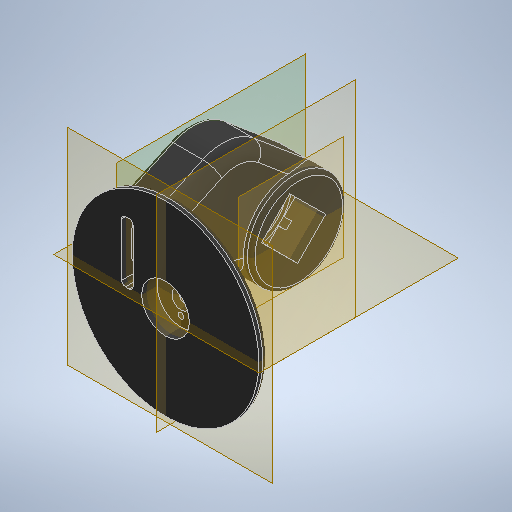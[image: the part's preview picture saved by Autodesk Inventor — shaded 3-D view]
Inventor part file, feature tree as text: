
AUTODESK INVENTOR PART (.ipt)
format: ipt  version: 2025.1 (Build 291241020, 241B)  size: 604,160 bytes
history: native  units: mm
features: extrude x18, sketch x17, projected_geometry x6, fillet x5, plane x2, revolve x1, chamfer x1
ambient origin geometry x8: Origin, YZ Plane, XZ Plane, XY Plane, X Axis, Y Axis, Z Axis, Center Point
bodies: Body1 (feature_tree), Body2 (feature_tree)
feature tree (50):
  extrude  "Extrusion6"  Depth=5.0mm TaperAngle=0.0deg
  extrude  "Extrusion15"  Depth=35.0mm
  extrude  "Extrusion16"  Depth=8.1mm TaperAngle=0.0deg
  extrude  "Extrusion17"  Depth=3.0mm
  revolve  "Revolution2"  [1 undecoded]
  fillet  "Fillet8"  Radius=4.75mm
  extrude  "Extrusion18"  Depth=3.0mm
  plane  "Work Plane5"
  extrude  "Extrusion19"  Depth=65.0mm
  extrude  "Extrusion20"  [1 undecoded]
  extrude  "Extrusion21"  Depth=10.0mm TaperAngle=0.0deg
  extrude  "Extrusion22"  Depth=35.0mm
  extrude  "Extrusion23"  Depth=20.071286mm
  extrude  "Extrusion24"  Depth=10.0mm TaperAngle=0.0deg
  extrude  "Extrusion25"  Depth=15.0mm
  extrude  "Extrusion26"  Depth=10.0mm
  sketch  "Sketch30"  dims[d126=42.0mm d128=36.0mm]
  extrude  "Extrusion27"  Depth=36.0mm
  extrude  "Extrusion28"  Depth=15.0mm
  plane  "Work Plane6"
  extrude  "Extrusion29"  Depth=2.0mm
  fillet  "Fillet9"  Radius=21.0mm
  chamfer  "Chamfer2"  Distance=7.9mm
  fillet  "Fillet10"  Radius=11.0mm
  fillet  "Fillet11"  Radius=10.0mm
  sketch  "Sketch32"  dims[d132=12.5mm d133=0.0mm d135=41.0mm d136=21.0mm d137=7.9mm d138=11.0mm d139=10.0mm d140=0.0mm d141=14.253mm d142=0.0mm d143=0.0mm d144=10.0mm d145=2.6mm d146=3.5mm d147=4.0mm d148=7.5mm d149=4.0mm d150=0.0mm d151=7.5mm d152=0.0mm d153=-2.5mm d154=2.5mm d155=2.0mm d156=0.0mm d157=5.6mm d158=2.0mm d159=45.0deg d160=7.0mm d161=2.0mm d162=7.0mm d165=1.0mm d166=32.0mm d167=0.0mm d168=0.0mm d169=15.0mm d170=0.0mm d171=2.0mm d134=0.5mm]
  extrude  "Extrusion30"  Depth=2.0mm
  extrude  "Extrusion31"  TaperAngle=0.0deg  [1 undecoded]
  fillet  "Fillet12"  Radius=10.0mm
  sketch  "Sketch8"  dims[d28=98.0mm d30=5.0mm d31=0.0mm]
  sketch  "Sketch16"  dims[d90=5.6mm d91=0.0mm d92=35.0mm]
  sketch  "Sketch17"  dims[d93=25.0mm d94=8.1mm d95=0.0mm]
  sketch  "Sketch18"  dims[d96=7.0mm d97=3.0mm]
  sketch  "Sketch19"  dims[d98=14.5mm d99=8.1mm d100=0.0mm d101=4.75mm]
  sketch  "Sketch20"  dims[d102=90.0deg d103=3.0mm]
  sketch  "Sketch21"  dims[d104=50.0mm d105=65.0mm]
  sketch  "Sketch22"  dims[d106=28.5mm d107=0.0mm d108=-4.0mm]
  projected_geometry  "Projected Loop2"
  sketch  "Sketch23"  dims[d109=28.5mm d110=0.0mm d111=10.0mm d112=0.0mm]
  sketch  "Sketch25"  dims[d113=8.726646mm d114=35.0mm]
  projected_geometry  "Projected Loop3"
  sketch  "Sketch26"  dims[d115=25.0mm d116=20.071286mm]
  projected_geometry  "Projected Loop4"
  sketch  "Sketch27"  dims[d117=10.0mm d118=0.0mm d119=10.0mm d120=0.0mm]
  projected_geometry  "Projected Loop5"
  sketch  "Sketch28"  dims[d121=11.34464mm d122=15.0mm]
  projected_geometry  "Projected Loop6"
  sketch  "Sketch29"  dims[d123=10.0mm d124=0.0mm d125=41.0mm]
  projected_geometry  "Projected Loop7"
  sketch  "Sketch31"  dims[d129=17.0mm d131=15.0mm]
note: 3 required parameter values undecoded (feature->parameter linkage not recoverable at this tier; creation-order binding heuristic only, values carry confidence <= 0.55)